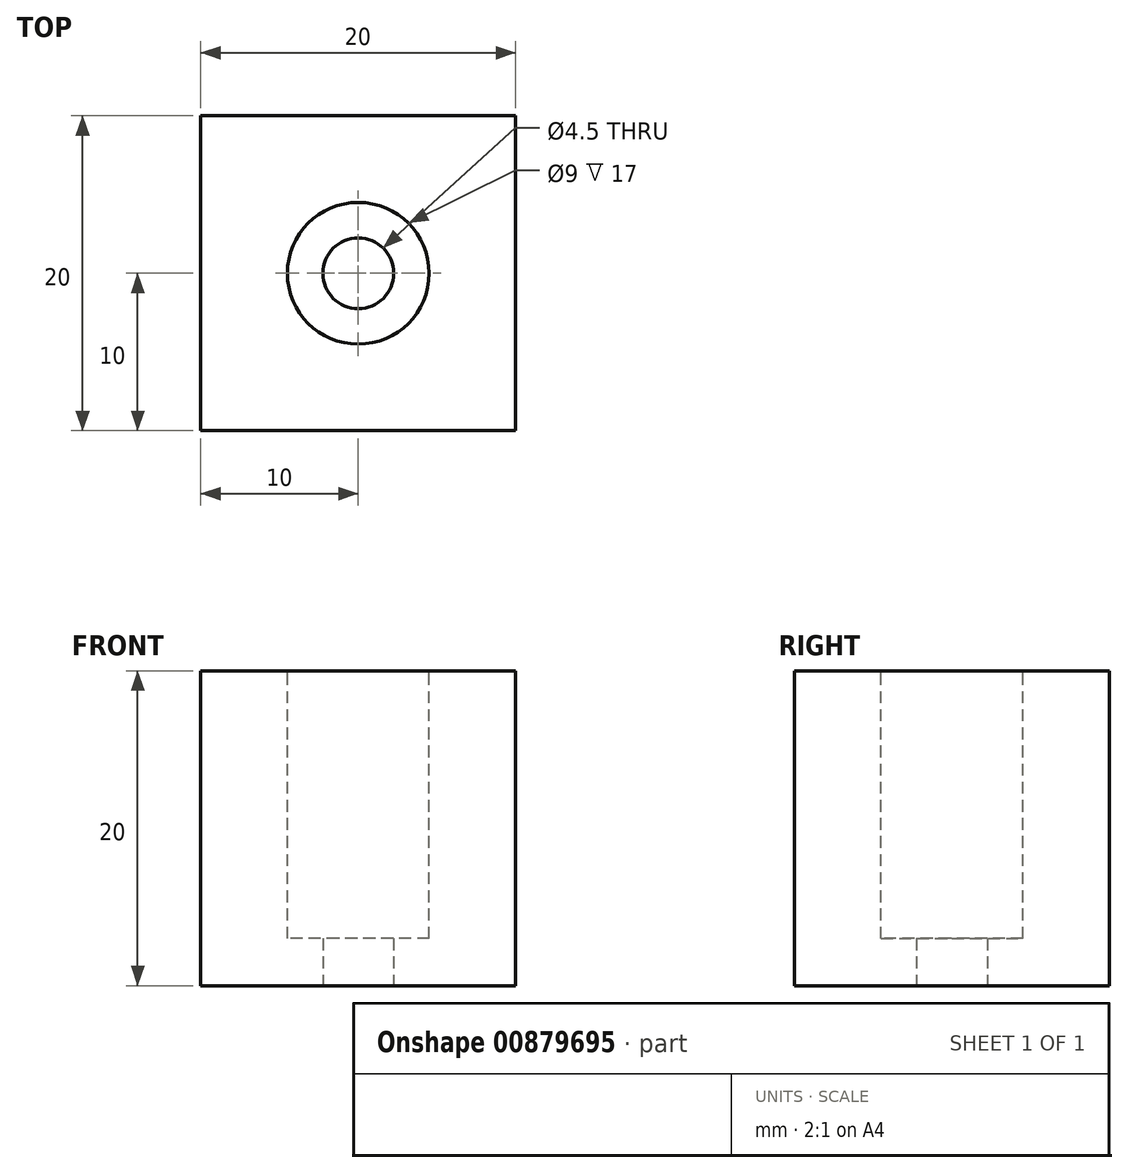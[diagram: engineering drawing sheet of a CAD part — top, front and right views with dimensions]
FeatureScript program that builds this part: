
annotation { "Feature Type Name" : "Feature", "Feature Type Description" : "" }
export const myFeature = defineFeature(function(context is Context, id is Id, definition is map)
    precondition{}
    {
        {
            var Q0;
            Q0=qCreatedBy(makeId("Top.planeOp"),FACE);
            var sketch = newSketch(context, id + "F0", { "sketchPlane" : qUnion([Q0])});
            skLineSegment(sketch, "E0.bottom", {"start": v(10, -10) * mm, "end": v(-10, -10) * mm});
            skLineSegment(sketch, "E0.top", {"start": v(10, 10) * mm, "end": v(-10, 10) * mm});
            skLineSegment(sketch, "E0.left", {"start": v(10, -10) * mm, "end": v(10, 10) * mm});
            skLineSegment(sketch, "E0.right", {"start": v(-10, -10) * mm, "end": v(-10, 10) * mm});
            skPoint(sketch, "E0.middle", {"position": v(0, 0) * mm});
            skCircle(sketch, "E1", {"center": v(0, 0) * mm, "radius": 2.25 * mm});
            skSolve(sketch);
        }
        {
            var Q0;
            Q0=makeQuery(id+"F0.imprint","IMPRINT",FACE,{"disambiguationData":[TD([[makeQuery(id+"F0.imprint","IMPRINT",EDGE,{"derivedFrom":sQuery(id+"F0.wireOp",EDGE,"E0.bottom")}),-1.0]])]});
            extrude(context, id + "F1", {"entities" : qUnion([Q0]), "depth" : 20 * mm, "offsetDistance" : 25 * mm});
        }
        {
            var Q0;
            Q0=makeQuery(id+"F1.opExtrude","CAP_FACE",FACE,{"disambiguationData":[OSD([sQuery(id+"F0.wireOp",EDGE,"E0.bottom"),sQuery(id+"F0.wireOp",EDGE,"E0.top"),sQuery(id+"F0.wireOp",EDGE,"E0.left"),sQuery(id+"F0.wireOp",EDGE,"E0.right"),sQuery(id+"F0.wireOp",EDGE,"E1")])],"isStart":false});
            var sketch = newSketch(context, id + "F2", { "sketchPlane" : qUnion([Q0])});
            skCircle(sketch, "E2", {"center": v(0, 0) * mm, "radius": 4.5 * mm});
            skSolve(sketch);
        }
        {
            var Q0;
            Q0=makeQuery(id+"F2.imprint","IMPRINT",FACE,{"disambiguationData":[TD([[makeQuery(id+"F2.imprint","IMPRINT",EDGE,{"derivedFrom":sQuery(id+"F2.wireOp",EDGE,"E2")}),1.0]])]});
            extrude(context, id + "F3", {"entities" : qUnion([Q0]), "operationType" : NewBodyOperationType.REMOVE, "oppositeDirection" : true, "depth" : 17 * mm, "offsetDistance" : 25 * mm});
        }
    });
